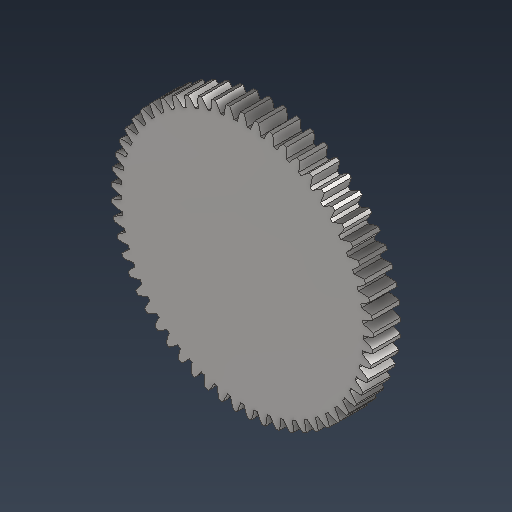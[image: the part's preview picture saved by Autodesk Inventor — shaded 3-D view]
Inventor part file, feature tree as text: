
AUTODESK INVENTOR PART (.ipt)
format: ipt  version: 2021 (Build 250183000, 183)  size: 391,168 bytes
history: native  units: mm (DEFAULTED — no unit token found)
features: plane x3, other x3, sketch x2, extrude x1
ambient origin geometry x8: Origin, YZ Plane, XZ Plane, XY Plane, X Axis, Y Axis, Z Axis, Center Point
bodies: Solid1 (feature_tree)
feature tree (9):
  extrude  "Extrusion1"  Depth=0.5mm TaperAngle=0.0deg
  plane  "Work Plane2"
  plane  "Work Plane8"
  plane  "Work Plane9"
  other  "Engrenagem reta"
  sketch  "Sketch1"  dims[d0=4.776mm d1=0.5mm d2=0.0mm]
  sketch  "Sketch2"  dims[d3=4.56mm d4=10.0mm d5=0.0mm d16=3.188mm d17=0.0mm d34=0.551157mm d39=0.0mm d41=0.0mm d43=3.188mm d46=3.188mm d47=0.0mm d48=0.0mm]
  other  "Srf1"
  other  "Diâmetro do flanco"
